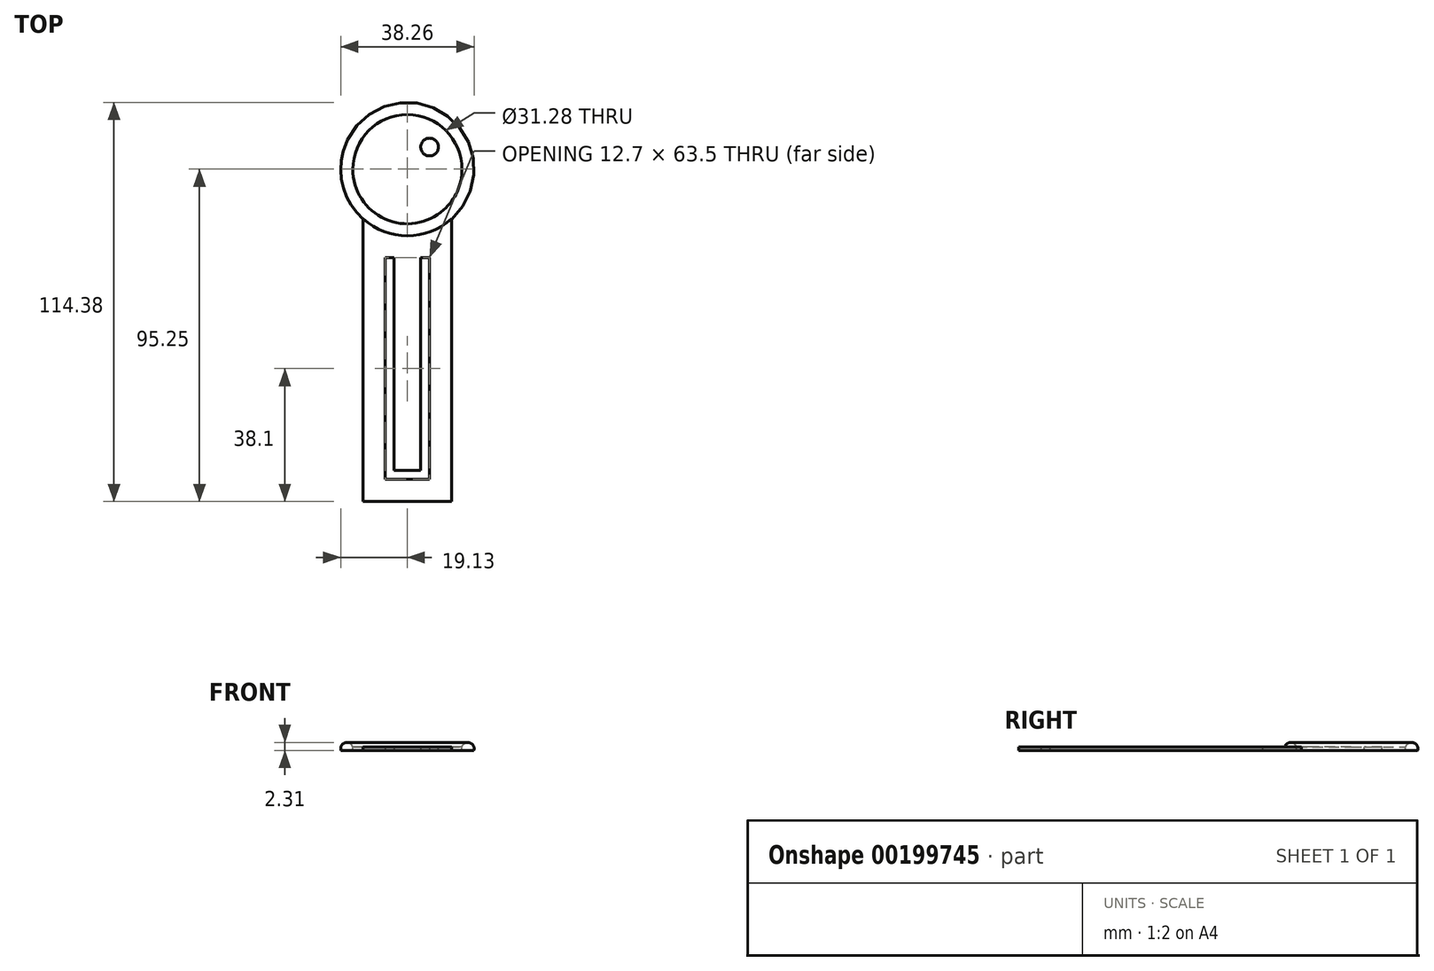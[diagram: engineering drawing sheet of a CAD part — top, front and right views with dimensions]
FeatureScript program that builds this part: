
annotation { "Feature Type Name" : "Feature", "Feature Type Description" : "" }
export const myFeature = defineFeature(function(context is Context, id is Id, definition is map)
    precondition{}
    {
        {
            var Q0;
            Q0=qCreatedBy(makeId("Top.planeOp"),FACE);
            var sketch = newSketch(context, id + "F0", { "sketchPlane" : qUnion([Q0])});
            skLineSegment(sketch, "E0.bottom", {"start": v(12.7, 38.1) * mm, "end": v(-12.7, 38.1) * mm});
            skLineSegment(sketch, "E0.top", {"start": v(12.7, -38.1) * mm, "end": v(-12.7, -38.1) * mm});
            skLineSegment(sketch, "E0.left", {"start": v(12.7, 38.1) * mm, "end": v(12.7, -38.1) * mm});
            skLineSegment(sketch, "E0.right", {"start": v(-12.7, 38.1) * mm, "end": v(-12.7, -38.1) * mm});
            skLineSegment(sketch, "E1.bottom", {"start": v(-6.35, 31.75) * mm, "end": v(6.35, 31.75) * mm});
            skLineSegment(sketch, "E1.top", {"start": v(-6.35, -31.75) * mm, "end": v(6.35, -31.75) * mm});
            skLineSegment(sketch, "E1.left", {"start": v(-6.35, 31.75) * mm, "end": v(-6.35, -31.75) * mm});
            skLineSegment(sketch, "E1.right", {"start": v(6.35, 31.75) * mm, "end": v(6.35, -31.75) * mm});
            skPoint(sketch, "E1.middle", {"position": v(0, 0) * mm});
            skLineSegment(sketch, "E2.top", {"start": v(-3.81, -29.21) * mm, "end": v(3.8, -29.21) * mm});
            skLineSegment(sketch, "E2.left", {"start": v(-3.8, 29.21) * mm, "end": v(-3.81, -29.21) * mm});
            skLineSegment(sketch, "E2.right", {"start": v(3.81, 29.21) * mm, "end": v(3.8, -29.21) * mm});
            skLineSegment(sketch, "E3", {"start": v(-3.8, 29.21) * mm, "end": v(-3.8, 31.75) * mm});
            skLineSegment(sketch, "E4", {"start": v(3.81, 29.21) * mm, "end": v(3.81, 31.75) * mm});
            skSolve(sketch);
        }
        {
            var Q0;
            Q0=makeQuery(id+"F0.imprint","IMPRINT",FACE,{"disambiguationData":[TD([[makeQuery(id+"F0.imprint","IMPRINT",EDGE,{"derivedFrom":sQuery(id+"F0.wireOp",EDGE,"E0.bottom")}),1.0]])]});
            var Q1;
            Q1=makeQuery(id+"F0.imprint","IMPRINT",FACE,{"disambiguationData":[TD([[makeQuery(id+"F0.imprint","IMPRINT",EDGE,{"derivedFrom":sQuery(id+"F0.wireOp",EDGE,"E2.top")}),1.0]])]});
            extrude(context, id + "F1", {"entities" : qUnion([Q0, Q1]), "depth" : 1 * mm});
        }
        {
            var Q0;
            Q0=qCreatedBy(makeId("Top.planeOp"),FACE);
            var sketch = newSketch(context, id + "F2", { "sketchPlane" : qUnion([Q0])});
            skCircle(sketch, "E5", {"center": v(0, 57.15) * mm, "radius": 19.05 * mm});
            skLineSegment(sketch, "E6.top", {"start": v(-12.7, 33.25) * mm, "end": v(12.7, 33.25) * mm});
            skLineSegment(sketch, "E6.left", {"start": v(-12.7, 42.95) * mm, "end": v(-12.7, 33.25) * mm});
            skLineSegment(sketch, "E6.right", {"start": v(12.7, 42.95) * mm, "end": v(12.7, 33.25) * mm});
            skPoint(sketch, "E6.middle", {"position": v(0, 38.1) * mm});
            skLineSegment(sketch, "E7", {"start": v(0, 57.15) * mm, "end": v(-19.05, 57.15) * mm});
            skSolve(sketch);
        }
        {
            var Q0;
            {var subQ0=sQuery(id+"F2.wireOp",EDGE,"E5");var subQ1=makeQuery(id+"F2.imprint","INTERSECT",VERTEX,{"derivedFrom":[subQ0,sQuery(id+"F2.wireOp",EDGE,"E6.left")]});Q0=makeQuery(id+"F2.imprint","IMPRINT",FACE,{"disambiguationData":[TD([[makeQuery(id+"F2.imprint","IMPRINT",EDGE,{"disambiguationData":[TD([[subQ1,-1.0]])],"derivedFrom":subQ0}),1.0]])]});}
            var Q1;
            Q1=makeQuery(id+"F2.imprint","IMPRINT",FACE,{"disambiguationData":[TD([[makeQuery(id+"F2.imprint","IMPRINT",EDGE,{"derivedFrom":sQuery(id+"F2.wireOp",EDGE,"E6.top")}),1.0]])]});
            extrude(context, id + "F3", {"entities" : qUnion([Q0, Q1]), "operationType" : NewBodyOperationType.ADD, "depth" : 1 * mm});
        }
        {
            var Q0;
            Q0=qCreatedBy(makeId("Front.planeOp"),FACE);
            cPlane(context, id + "F4", {"entities" : qUnion([Q0]), "cplaneType" : CPlaneType.OFFSET, "offset" : 57.15 * mm, "oppositeDirection" : true, "width" : 152.4 * mm, "height" : 152.4 * mm});
        }
        {
            var Q0;
            Q0=qCreatedBy(id+"F4.planeOp",FACE);
            var sketch = newSketch(context, id + "F5", { "sketchPlane" : qUnion([Q0])});
            skArc(sketch, "E8", {"start": v(-15.66, 0) * mm, "mid": v(-17.35, 2.3) * mm, "end": v(-19.05, 0) * mm});
            skLineSegment(sketch, "E9", {"start": v(-19.05, 0) * mm, "end": v(-15.66, 0) * mm});
            skSolve(sketch);
        }
        {
            var Q0;
            Q0=makeQuery(id+"F3.boolean.opBoolean","MERGE",FACE,{"derivedFrom":[makeQuery(id+"F1.opExtrude","CAP_FACE",FACE,{"disambiguationData":[OSD([sQuery(id+"F0.wireOp",EDGE,"E0.bottom"),sQuery(id+"F0.wireOp",EDGE,"E0.top"),sQuery(id+"F0.wireOp",EDGE,"E0.left"),sQuery(id+"F0.wireOp",EDGE,"E0.right"),sQuery(id+"F0.wireOp",EDGE,"E1.bottom"),sQuery(id+"F0.wireOp",EDGE,"E1.top"),sQuery(id+"F0.wireOp",EDGE,"E1.left"),sQuery(id+"F0.wireOp",EDGE,"E1.right"),sQuery(id+"F0.wireOp",EDGE,"E2.top"),sQuery(id+"F0.wireOp",EDGE,"E2.left"),sQuery(id+"F0.wireOp",EDGE,"E2.right"),sQuery(id+"F0.wireOp",EDGE,"E3"),sQuery(id+"F0.wireOp",EDGE,"E4")])],"isStart":false}),makeQuery(id+"F3.opExtrude","CAP_FACE",FACE,{"disambiguationData":[OSD([sQuery(id+"F2.wireOp",EDGE,"E5"),sQuery(id+"F2.wireOp",EDGE,"E6.top"),sQuery(id+"F2.wireOp",EDGE,"E6.left"),sQuery(id+"F2.wireOp",EDGE,"E6.right")])],"isStart":false})]});
            var sketch = newSketch(context, id + "F6", { "sketchPlane" : qUnion([Q0])});
            skCircle(sketch, "E10", {"center": v(0, 57.15) * mm, "radius": 19.05 * mm});
            skSolve(sketch);
        }
        {
            var Q0;
            Q0 = qSketchRegion(id + "F5", true);
            var Q1;
            Q1 = qConstructionFilter(qBodyType(qCreatedBy(id + "F6" ,EDGE), BodyType.WIRE), ConstructionObject.NO);
            sweep(context, id + "F7", {"operationType" : NewBodyOperationType.ADD, "profiles" : qUnion([Q0]), "path" : qUnion([Q1])});
        }
        {
            var Q0;
            Q0=makeQuery(id+"F7.boolean.opBoolean","SPLIT",FACE,{"disambiguationData":[TD([makeQuery(id+"F7.opSweep","SWEPT_FACE",FACE,{"disambiguationData":[OSD([sQuery(id+"F5.wireOp",EDGE,"E8"),sQuery(id+"F6.wireOp",EDGE,"E10")])]})])],"derivedFrom":makeQuery(id+"F3.boolean.opBoolean","MERGE",FACE,{"derivedFrom":[makeQuery(id+"F1.opExtrude","CAP_FACE",FACE,{"disambiguationData":[OSD([sQuery(id+"F0.wireOp",EDGE,"E0.bottom"),sQuery(id+"F0.wireOp",EDGE,"E0.top"),sQuery(id+"F0.wireOp",EDGE,"E0.left"),sQuery(id+"F0.wireOp",EDGE,"E0.right"),sQuery(id+"F0.wireOp",EDGE,"E1.bottom"),sQuery(id+"F0.wireOp",EDGE,"E1.top"),sQuery(id+"F0.wireOp",EDGE,"E1.left"),sQuery(id+"F0.wireOp",EDGE,"E1.right"),sQuery(id+"F0.wireOp",EDGE,"E2.top"),sQuery(id+"F0.wireOp",EDGE,"E2.left"),sQuery(id+"F0.wireOp",EDGE,"E2.right"),sQuery(id+"F0.wireOp",EDGE,"E3"),sQuery(id+"F0.wireOp",EDGE,"E4")])],"isStart":false}),makeQuery(id+"F3.opExtrude","CAP_FACE",FACE,{"disambiguationData":[OSD([sQuery(id+"F2.wireOp",EDGE,"E5"),sQuery(id+"F2.wireOp",EDGE,"E6.top"),sQuery(id+"F2.wireOp",EDGE,"E6.left"),sQuery(id+"F2.wireOp",EDGE,"E6.right")])],"isStart":false})]})});
            var sketch = newSketch(context, id + "F8", { "sketchPlane" : qUnion([Q0])});
            skCircle(sketch, "E11", {"center": v(-6.35, 63.5) * mm, "radius": 2.54 * mm});
            skCircle(sketch, "E12.MirrorC", {"center": v(6.35, 63.5) * mm, "radius": 2.54 * mm});
            skSolve(sketch);
        }
        {
            var Q0;
            Q0=makeQuery(id+"F8.imprint","IMPRINT",FACE,{"disambiguationData":[TD([[makeQuery(id+"F8.imprint","IMPRINT",EDGE,{"derivedFrom":sQuery(id+"F8.wireOp",EDGE,"E11")}),1.0]])]});
            var Q1;
            Q1=makeQuery(id+"F8.imprint","IMPRINT",FACE,{"disambiguationData":[TD([[makeQuery(id+"F8.imprint","IMPRINT",EDGE,{"derivedFrom":sQuery(id+"F8.wireOp",EDGE,"E12.MirrorC")}),-1.0]])]});
            extrude(context, id + "F9", {"entities" : qUnion([Q0, Q1]), "operationType" : NewBodyOperationType.REMOVE, "endBound" : BoundingType.THROUGH_ALL, "oppositeDirection" : true, "depth" : 25.4 * mm});
        }
        {
            var Q0;
            Q0=makeQuery(id+"F7.boolean.opBoolean","SPLIT",FACE,{"disambiguationData":[TD([makeQuery(id+"F7.opSweep","SWEPT_FACE",FACE,{"disambiguationData":[OSD([sQuery(id+"F5.wireOp",EDGE,"E8"),sQuery(id+"F6.wireOp",EDGE,"E10")])]})])],"derivedFrom":makeQuery(id+"F3.boolean.opBoolean","MERGE",FACE,{"derivedFrom":[makeQuery(id+"F1.opExtrude","CAP_FACE",FACE,{"disambiguationData":[OSD([sQuery(id+"F0.wireOp",EDGE,"E0.bottom"),sQuery(id+"F0.wireOp",EDGE,"E0.top"),sQuery(id+"F0.wireOp",EDGE,"E0.left"),sQuery(id+"F0.wireOp",EDGE,"E0.right"),sQuery(id+"F0.wireOp",EDGE,"E1.bottom"),sQuery(id+"F0.wireOp",EDGE,"E1.top"),sQuery(id+"F0.wireOp",EDGE,"E1.left"),sQuery(id+"F0.wireOp",EDGE,"E1.right"),sQuery(id+"F0.wireOp",EDGE,"E2.top"),sQuery(id+"F0.wireOp",EDGE,"E2.left"),sQuery(id+"F0.wireOp",EDGE,"E2.right"),sQuery(id+"F0.wireOp",EDGE,"E3"),sQuery(id+"F0.wireOp",EDGE,"E4")])],"isStart":false}),makeQuery(id+"F3.opExtrude","CAP_FACE",FACE,{"disambiguationData":[OSD([sQuery(id+"F2.wireOp",EDGE,"E5"),sQuery(id+"F2.wireOp",EDGE,"E6.top"),sQuery(id+"F2.wireOp",EDGE,"E6.left"),sQuery(id+"F2.wireOp",EDGE,"E6.right")])],"isStart":false})]})});
            var sketch = newSketch(context, id + "F10", { "sketchPlane" : qUnion([Q0])});
            skArc(sketch, "E13", {"start": v(-10.16, 57.15) * mm, "mid": v(0, 47) * mm, "end": v(10.16, 57.15) * mm});
            skArc(sketch, "E14", {"start": v(-10.16, 57.15) * mm, "mid": v(0, 51.48) * mm, "end": v(10.16, 57.15) * mm});
            skSolve(sketch);
        }
        {
            var Q0;
            Q0=makeQuery(id+"F10.imprint","IMPRINT",FACE,{"disambiguationData":[TD([[makeQuery(id+"F10.imprint","IMPRINT",EDGE,{"derivedFrom":sQuery(id+"F10.wireOp",EDGE,"E13")}),1.0]])]});
            extrude(context, id + "F11", {"entities" : qUnion([Q0]), "operationType" : NewBodyOperationType.REMOVE, "endBound" : BoundingType.THROUGH_ALL, "oppositeDirection" : true, "depth" : 25.4 * mm});
        }
    });
